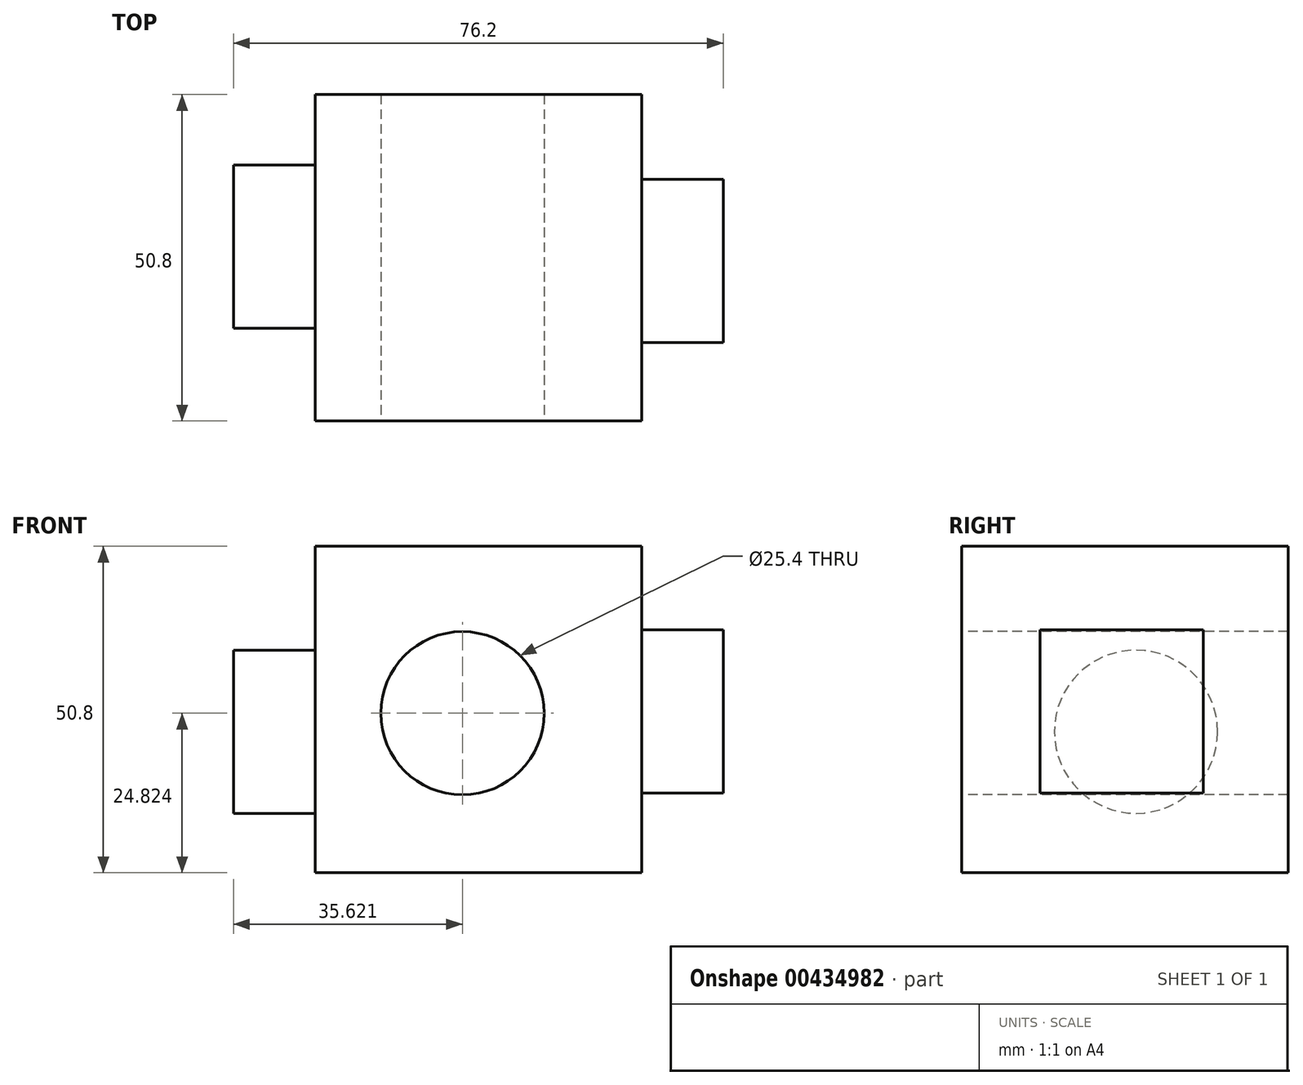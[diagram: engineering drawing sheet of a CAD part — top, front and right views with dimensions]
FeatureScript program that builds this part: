
annotation { "Feature Type Name" : "Feature", "Feature Type Description" : "" }
export const myFeature = defineFeature(function(context is Context, id is Id, definition is map)
    precondition{}
    {
        {
            var Q0;
            Q0=qCreatedBy(makeId("Front.planeOp"),FACE);
            var sketch = newSketch(context, id + "F0", { "sketchPlane" : qUnion([Q0])});
            skLineSegment(sketch, "E0.bottom", {"start": v(0, 0) * mm, "end": v(-50.8, 0) * mm});
            skLineSegment(sketch, "E0.top", {"start": v(0, 0) * mm, "end": v(-50.8, 0) * mm});
            skLineSegment(sketch, "E0.left", {"start": v(0, 0) * mm, "end": v(0, 0) * mm});
            skLineSegment(sketch, "E0.right", {"start": v(-50.8, 0) * mm, "end": v(-50.8, 0) * mm});
            skLineSegment(sketch, "E1", {"start": v(-50.8, 0) * mm, "end": v(-50.8, 50.8) * mm});
            skLineSegment(sketch, "E2", {"start": v(-50.8, 50.8) * mm, "end": v(0, 50.8) * mm});
            skLineSegment(sketch, "E3", {"start": v(0, 50.8) * mm, "end": v(0, 0) * mm});
            skSolve(sketch);
        }
        {
            var Q0;
            Q0 = qSketchRegion(id + "F0", true);
            extrude(context, id + "F1", {"entities" : qUnion([Q0]), "depth" : 50.8 * mm});
        }
        {
            var Q0;
            Q0=makeQuery(id+"F1.opExtrude","CAP_FACE",FACE,{"disambiguationData":[OSD([sQuery(id+"F0.wireOp",EDGE,"E0.top"),sQuery(id+"F0.wireOp",EDGE,"E1"),sQuery(id+"F0.wireOp",EDGE,"E2"),sQuery(id+"F0.wireOp",EDGE,"E3")])],"isStart":false});
            var sketch = newSketch(context, id + "F2", { "sketchPlane" : qUnion([Q0])});
            skCircle(sketch, "E4", {"center": v(-27.88, 24.82) * mm, "radius": 12.7 * mm});
            skSolve(sketch);
        }
        {
            var Q0;
            Q0 = qSketchRegion(id + "F2", true);
            extrude(context, id + "F3", {"entities" : qUnion([Q0]), "operationType" : NewBodyOperationType.REMOVE, "oppositeDirection" : true, "depth" : 50.8 * mm});
        }
        {
            var Q0;
            Q0=makeQuery(id+"F1.opExtrude","SWEPT_FACE",FACE,{"disambiguationData":[OSD([sQuery(id+"F0.wireOp",EDGE,"E1")])]});
            var sketch = newSketch(context, id + "F4", { "sketchPlane" : qUnion([Q0])});
            skCircle(sketch, "E5", {"center": v(23.68, 21.96) * mm, "radius": 12.7 * mm});
            skSolve(sketch);
        }
        {
            var Q0;
            Q0 = qSketchRegion(id + "F4", true);
            extrude(context, id + "F5", {"entities" : qUnion([Q0]), "operationType" : NewBodyOperationType.ADD, "depth" : 12.7 * mm});
        }
        {
            var Q0;
            Q0=makeQuery(id+"F1.opExtrude","SWEPT_FACE",FACE,{"disambiguationData":[OSD([sQuery(id+"F0.wireOp",EDGE,"E3")])]});
            var sketch = newSketch(context, id + "F6", { "sketchPlane" : qUnion([Q0])});
            skSolve(sketch);
        }
        {
            var Q0;
            {var subQ0=sQuery(id+"F0.wireOp",EDGE,"E3");Q0=makeQuery(id+"F6.imprint","IMPRINT",FACE,{"disambiguationData":[TD([[makeQuery(id+"F6.imprint","IMPRINT",EDGE,{"derivedFrom":makeQuery(id+"F1.opExtrude","CAP_EDGE",EDGE,{"disambiguationData":[OSD([subQ0])],"isStart":true})}),-1.0]])]});}
            var sketch = newSketch(context, id + "F7", { "sketchPlane" : qUnion([Q0])});
            skLineSegment(sketch, "E6.bottom", {"start": v(-38.58, 37.81) * mm, "end": v(-13.18, 37.81) * mm});
            skLineSegment(sketch, "E6.top", {"start": v(-38.58, 12.41) * mm, "end": v(-13.18, 12.41) * mm});
            skLineSegment(sketch, "E6.left", {"start": v(-38.58, 37.81) * mm, "end": v(-38.58, 12.41) * mm});
            skLineSegment(sketch, "E6.right", {"start": v(-13.18, 37.81) * mm, "end": v(-13.18, 12.41) * mm});
            skSolve(sketch);
        }
        {
            var Q0;
            Q0=makeQuery(id+"F7.imprint","IMPRINT",FACE,{"disambiguationData":[TD([[makeQuery(id+"F7.imprint","IMPRINT",EDGE,{"derivedFrom":sQuery(id+"F7.wireOp",EDGE,"E6.bottom")}),-1.0]])]});
            extrude(context, id + "F8", {"entities" : qUnion([Q0]), "operationType" : NewBodyOperationType.ADD, "depth" : 12.7 * mm});
        }
    });
